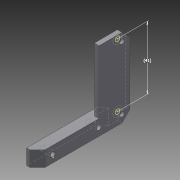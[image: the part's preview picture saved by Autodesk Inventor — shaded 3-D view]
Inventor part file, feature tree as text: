
AUTODESK INVENTOR PART (.ipt)
format: ipt  version: 2015 (Build 190159000, 159)  size: 137,216 bytes
history: native  units: mm
features: sketch x6, extrude x3, chamfer x3, hole x2
ambient origin geometry x8: Origin, YZ Plane, XZ Plane, XY Plane, X Axis, Y Axis, Z Axis, Center Point
bodies: Solid1 (feature_tree)
feature tree (14):
  extrude  "Extrusion1"  Depth=7.0mm
  hole  "Hole1"  [1 undecoded]
  chamfer  "Chamfer1"  Distance=5.0mm Angle=45.0deg
  extrude  "Extrusion2"  Depth=51.0mm
  extrude  "Extrusion3"  Depth=10.0mm
  hole  "Hole2"  [1 undecoded]
  chamfer  "Chamfer2"  Distance=7.0mm
  chamfer  "Chamfer3"  Distance=15.0mm
  sketch  "Sketch6"  dims[d8=3.0mm d9=6.0mm d10=4.0mm d11=2.0mm d12=90.0deg d13=7.0mm d14=20.594885mm d15=5.0mm d16=2.0mm d17=45.0deg d18=51.0mm d19=10.0mm d20=10.0mm d21=7.0mm d22=0.0mm d23=15.0mm d24=4.0mm d25=0.0mm d26=5.0mm d27=5.0mm d28=5.0mm d29=5.0mm d30=3.0mm d31=6.0mm d32=6.0mm d33=2.0mm d34=90.0deg d35=7.0mm d36=20.594885mm d37=5.0mm d38=2.0mm d39=45.0deg d40=4.0mm d41=2.0mm d42=45.0deg d43=41.0mm]
  sketch  "Sketch1"  dims[d0=7.0mm d1=50.0mm]
  sketch  "Sketch2"  dims[d2=10.0mm d3=0.0mm d4=10.0mm]
  sketch  "Sketch3"  dims[d5=5.0mm]
  sketch  "Sketch4"  dims[d6=5.0mm]
  sketch  "Sketch5"  dims[d7=30.0mm]
note: 2 required parameter values undecoded (feature->parameter linkage not recoverable at this tier; creation-order binding heuristic only, values carry confidence <= 0.55)
